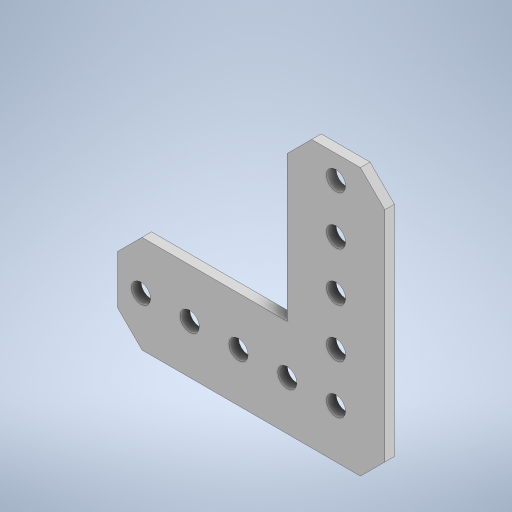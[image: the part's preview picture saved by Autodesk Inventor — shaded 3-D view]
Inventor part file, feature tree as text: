
AUTODESK INVENTOR PART (.ipt)
format: ipt  version: 2024.2 (Build 282272000, 272)  size: 255,488 bytes
history: native  units: in
note: dims shown in document units (in); Inventor stores cm internally (conversion verified against a paired STEP export)
features: chamfer x1
ambient origin geometry x8: Origin, YZ Plane, XZ Plane, XY Plane, X Axis, Y Axis, Z Axis, Center Point
bodies: Solid1 (feature_tree)
feature tree (1):
  chamfer  "Chamfer1"  [1 undecoded]
note: 1 required parameter value undecoded (feature->parameter linkage not recoverable at this tier; creation-order binding heuristic only, values carry confidence <= 0.55)
